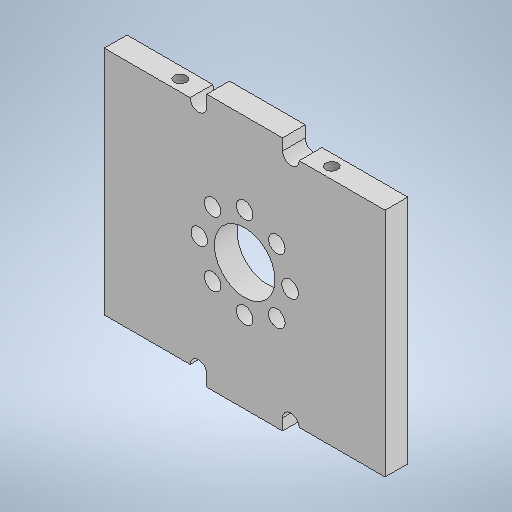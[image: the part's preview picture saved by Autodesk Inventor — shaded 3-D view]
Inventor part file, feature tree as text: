
AUTODESK INVENTOR PART (.ipt)
format: ipt  version: 2025.1 (Build 291241000, 241)  size: 276,480 bytes
history: native  units: mm
features: other x2, sketch x2, extrude x2, hole x1
ambient origin geometry x8: Origin, YZ Plane, XZ Plane, XY Plane, X Axis, Y Axis, Z Axis, Center Point
bodies: Body1 (feature_tree)
feature tree (7):
  other  "ソリッド1"
  sketch  "スケッチ1"
  extrude  "押し出し1"  Depth=8.0mm
  extrude  "押し出し2"  Depth=12.0mm
  hole  "穴1"  [1 undecoded]
  other  "スケッチ円形状パターン1"
  sketch  "スケッチ2"
note: 1 required parameter value undecoded (feature->parameter linkage not recoverable at this tier; creation-order binding heuristic only, values carry confidence <= 0.55)
